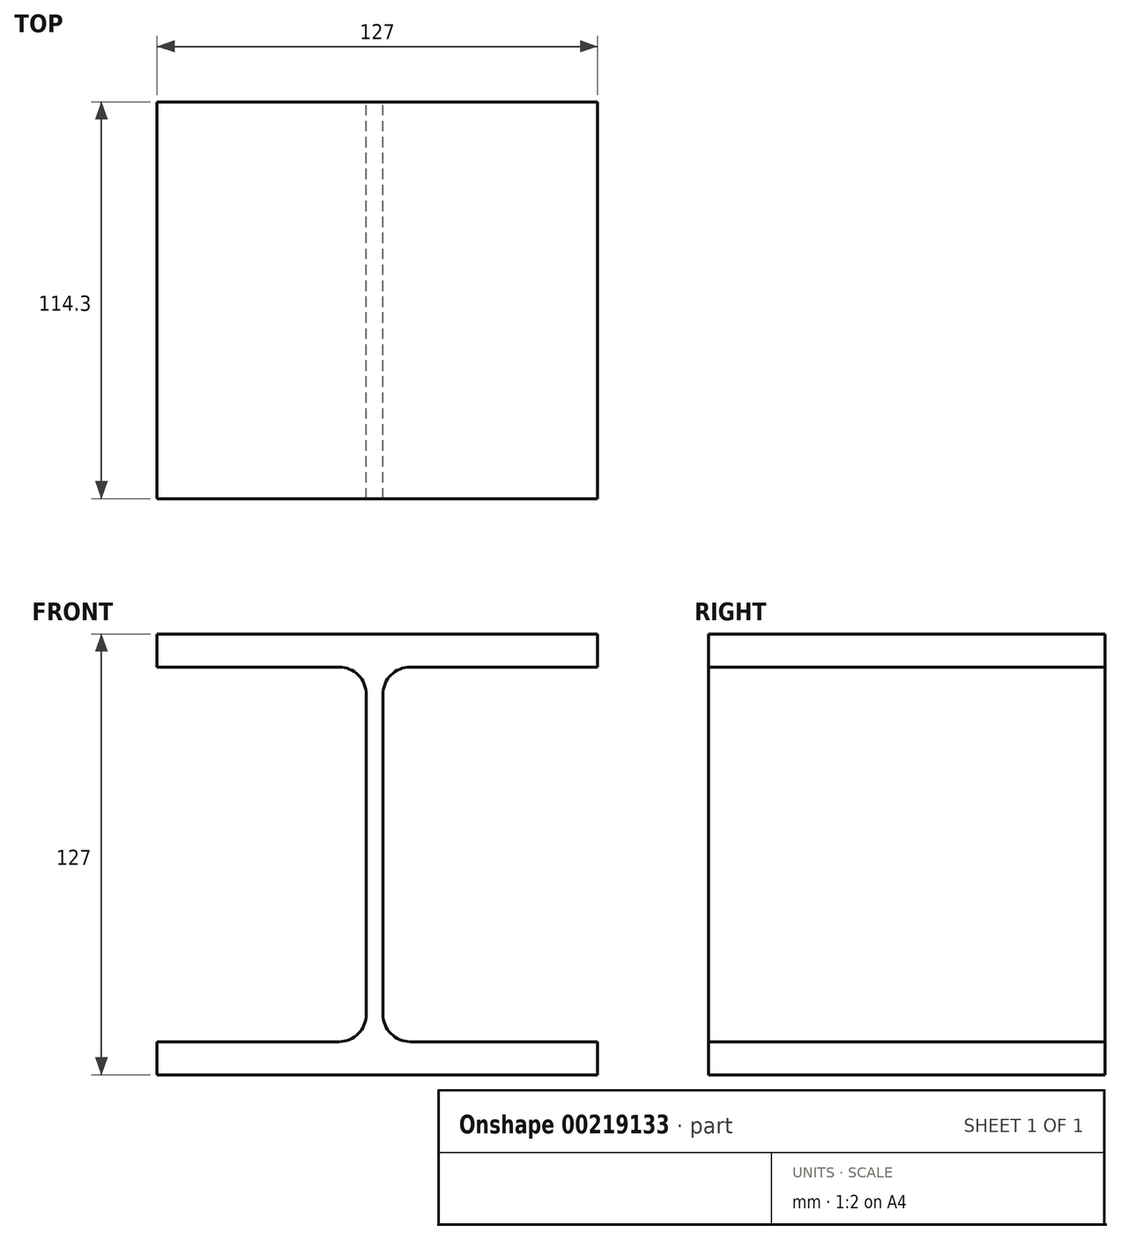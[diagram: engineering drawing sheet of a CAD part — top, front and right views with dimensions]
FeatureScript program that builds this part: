
annotation { "Feature Type Name" : "Feature", "Feature Type Description" : "" }
export const myFeature = defineFeature(function(context is Context, id is Id, definition is map)
    precondition{}
    {
        {
            var Q0;
            Q0=qCreatedBy(makeId("Front.planeOp"),FACE);
            var sketch = newSketch(context, id + "F0", { "sketchPlane" : qUnion([Q0])});
            skLineSegment(sketch, "E0", {"start": v(-48.66, 53.07) * mm, "end": v(78.34, 53.07) * mm});
            skLineSegment(sketch, "E1", {"start": v(78.34, 53.07) * mm, "end": v(78.34, 43.54) * mm});
            skLineSegment(sketch, "E2", {"start": v(78.34, 43.54) * mm, "end": v(24.37, 43.54) * mm});
            skLineSegment(sketch, "E3", {"start": v(-48.66, 43.54) * mm, "end": v(-48.66, 53.07) * mm});
            skLineSegment(sketch, "E4", {"start": v(-48.66, -73.93) * mm, "end": v(78.34, -73.93) * mm});
            skLineSegment(sketch, "E5", {"start": v(78.34, -73.93) * mm, "end": v(78.34, -64.4) * mm});
            skLineSegment(sketch, "E6", {"start": v(3.73, -64.4) * mm, "end": v(-48.66, -64.4) * mm});
            skLineSegment(sketch, "E7", {"start": v(16.43, 35.6) * mm, "end": v(16.43, -56.47) * mm});
            skLineSegment(sketch, "E8", {"start": v(11.67, 35.6) * mm, "end": v(11.67, -56.47) * mm});
            skPoint(sketch, "E9.newPointB", {"position": v(-48.66, 43.54) * mm});
            skArc(sketch, "E9.filletArc", {"start": v(24.37, 43.54) * mm, "mid": v(18.75, 41.22) * mm, "end": v(16.43, 35.6) * mm});
            skLineSegment(sketch, "E10", {"start": v(-48.66, 43.54) * mm, "end": v(3.73, 43.54) * mm});
            skArc(sketch, "E11.filletArc", {"start": v(11.67, 35.6) * mm, "mid": v(9.34, 41.22) * mm, "end": v(3.73, 43.54) * mm});
            skArc(sketch, "E12.filletArc", {"start": v(3.73, -64.4) * mm, "mid": v(9.34, -62.08) * mm, "end": v(11.67, -56.47) * mm});
            skLineSegment(sketch, "E13", {"start": v(78.34, -64.4) * mm, "end": v(24.37, -64.4) * mm});
            skArc(sketch, "E14.filletArc", {"start": v(16.43, -56.47) * mm, "mid": v(18.75, -62.08) * mm, "end": v(24.37, -64.4) * mm});
            skLineSegment(sketch, "E15", {"start": v(-48.66, -64.4) * mm, "end": v(-48.66, -73.93) * mm});
            skSolve(sketch);
        }
        {
            var Q0;
            Q0 = qSketchRegion(id + "F0", true);
            extrude(context, id + "F1", {"entities" : qUnion([Q0]), "depth" : 114.3 * mm});
        }
    });
